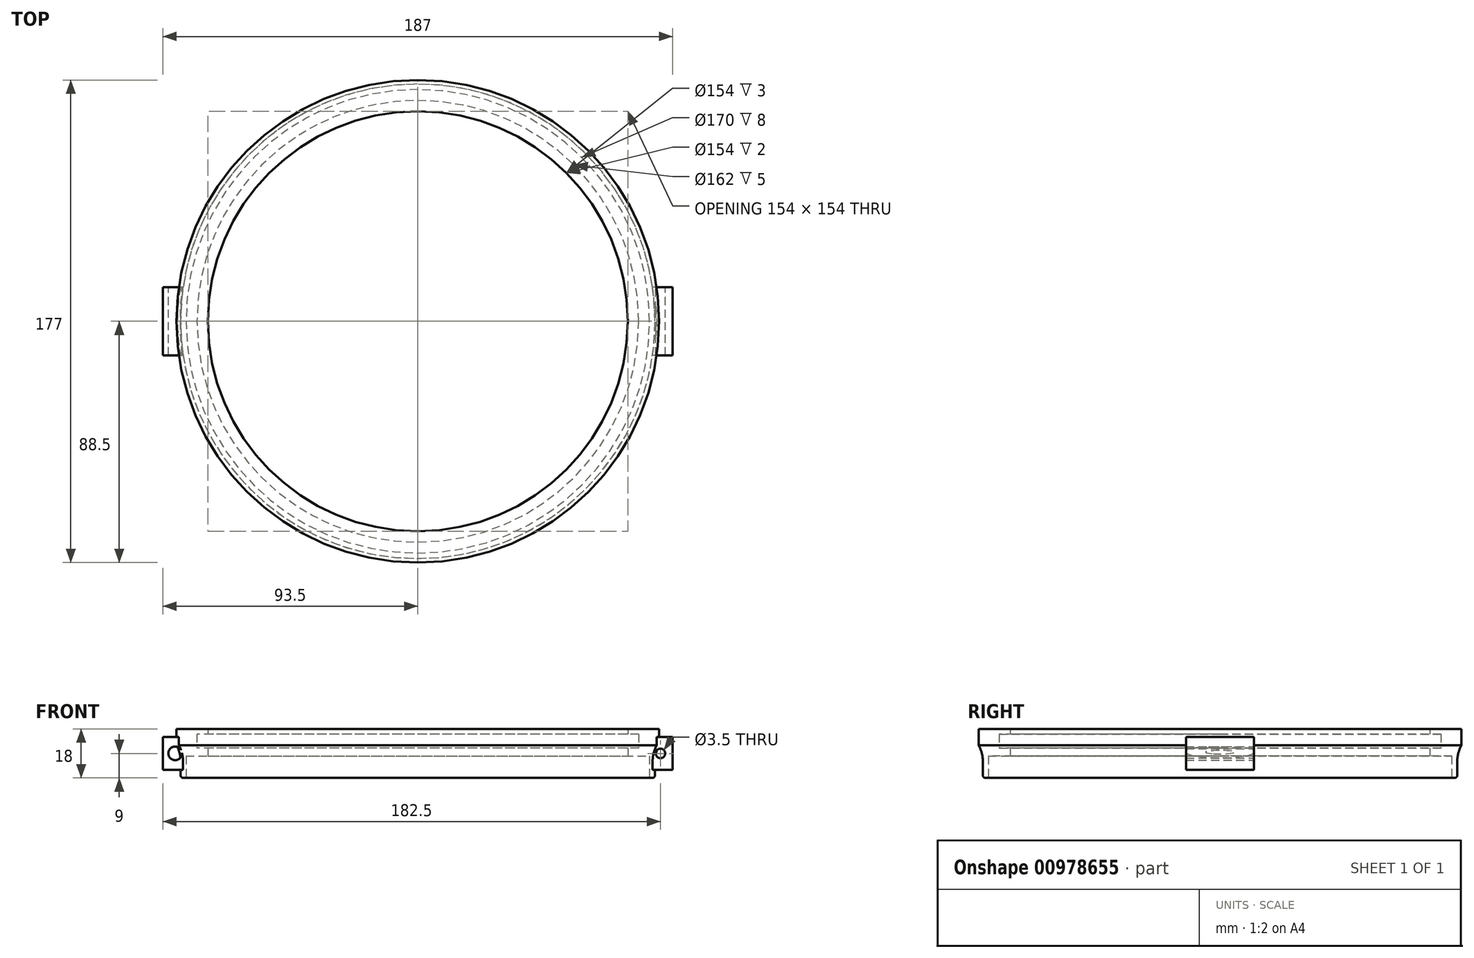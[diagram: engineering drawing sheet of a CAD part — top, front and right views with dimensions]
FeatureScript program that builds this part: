
annotation { "Feature Type Name" : "Feature", "Feature Type Description" : "" }
export const myFeature = defineFeature(function(context is Context, id is Id, definition is map)
    precondition{}
    {
        {
            var Q0;
            Q0=qCreatedBy(makeId("Front.planeOp"),FACE);
            var sketch = newSketch(context, id + "F0", { "sketchPlane" : qUnion([Q0])});
            skLineSegment(sketch, "E0", {"start": v(0, 0) * mm, "end": v(-84, 0) * mm});
            skLineSegment(sketch, "E1", {"start": v(-77, -3) * mm, "end": v(-85, -3) * mm});
            skLineSegment(sketch, "E2", {"start": v(-85, -3) * mm, "end": v(-85, -11) * mm});
            skLineSegment(sketch, "E3", {"start": v(-85, -11) * mm, "end": v(-87, -11) * mm});
            skLineSegment(sketch, "E4", {"start": v(-77, 7) * mm, "end": v(-88.5, 7) * mm});
            skLineSegment(sketch, "E5", {"start": v(-87, -11) * mm, "end": v(-87, -5) * mm});
            skLineSegment(sketch, "E6", {"start": v(-88.5, 7) * mm, "end": v(-88.5, 1) * mm});
            skArc(sketch, "E7", {"start": v(-87, -5) * mm, "mid": v(-87.38, -1.9) * mm, "end": v(-88.5, 1) * mm});
            skLineSegment(sketch, "E8", {"start": v(-77, 7) * mm, "end": v(-77, -3) * mm});
            skLineSegment(sketch, "E9", {"start": v(0, -15.27) * mm, "end": v(0, 14.73) * mm});
            skSolve(sketch);
        }
        {
            var Q0;
            Q0 = qSketchRegion(id + "F0", true);
            var Q1;
            Q1=sQuery(id+"F0.wireOp",EDGE,"E9");
            revolve(context, id + "F1", {"surfaceOperationType" : NewSurfaceOperationType.NEW, "entities" : qUnion([Q0]), "axis" : qUnion([Q1]), "revolveType" : RevolveType.FULL});
        }
        {
            var Q0;
            Q0=qCreatedBy(makeId("Top.planeOp"),FACE);
            var sketch = newSketch(context, id + "F2", { "sketchPlane" : qUnion([Q0])});
            skCircle(sketch, "E10", {"center": v(0, 0) * mm, "radius": 81 * mm});
            skSolve(sketch);
        }
        {
            var Q0;
            Q0 = qSketchRegion(id + "F2", true);
            extrude(context, id + "F3", {"entities" : qUnion([Q0]), "operationType" : NewBodyOperationType.REMOVE, "depth" : 5 * mm, "offsetDistance" : 25 * mm});
        }
        {
            var Q0;
            Q0=makeQuery(id+"F1.opRevolve","SWEPT_EDGE",EDGE,{"disambiguationData":[OSD([sQuery(id+"F0.wireOp",EDGE,"E3"),sQuery(id+"F0.wireOp",EDGE,"E5")])]});
            fillet(context, id + "F4", {"entities" : qUnion([Q0]), "radius" : 1 * mm, "tangentPropagation" : true, "allowEdgeOverflow" : false});
        }
        {
            var Q0;
            Q0=qCreatedBy(makeId("Front.planeOp"),FACE);
            var sketch = newSketch(context, id + "F5", { "sketchPlane" : qUnion([Q0])});
            skLineSegment(sketch, "E11.bottom", {"start": v(-85.5, 4) * mm, "end": v(-93.5, 4) * mm});
            skLineSegment(sketch, "E11.top", {"start": v(-85.5, -8) * mm, "end": v(-93.5, -8) * mm});
            skLineSegment(sketch, "E11.left", {"start": v(-85.5, 4) * mm, "end": v(-85.5, -8) * mm});
            skLineSegment(sketch, "E11.right", {"start": v(-93.5, 4) * mm, "end": v(-93.5, -8) * mm});
            skCircle(sketch, "E12", {"center": v(-89, -2) * mm, "radius": 2.5 * mm});
            skSolve(sketch);
        }
        {
            var Q0;
            Q0=qCreatedBy(makeId("Front.planeOp"),FACE);
            var sketch = newSketch(context, id + "F6", { "sketchPlane" : qUnion([Q0])});
            skLineSegment(sketch, "E13.bottom", {"start": v(93.5, 4) * mm, "end": v(85.5, 4) * mm});
            skLineSegment(sketch, "E13.top", {"start": v(93.5, -8) * mm, "end": v(85.5, -8) * mm});
            skLineSegment(sketch, "E13.left", {"start": v(93.5, 4) * mm, "end": v(93.5, -8) * mm});
            skLineSegment(sketch, "E13.right", {"start": v(85.5, 4) * mm, "end": v(85.5, -8) * mm});
            skCircle(sketch, "E14", {"center": v(89, -2) * mm, "radius": 1.75 * mm});
            skSolve(sketch);
        }
        {
            var Q0;
            Q0 = qSketchRegion(id + "F5", true);
            extrude(context, id + "F7", {"entities" : qUnion([Q0]), "operationType" : NewBodyOperationType.ADD, "endBound" : BoundingType.SYMMETRIC, "depth" : 25 * mm, "offsetDistance" : 25 * mm});
        }
        {
            var Q0;
            Q0 = qSketchRegion(id + "F6", true);
            extrude(context, id + "F8", {"entities" : qUnion([Q0]), "operationType" : NewBodyOperationType.ADD, "endBound" : BoundingType.SYMMETRIC, "depth" : 25 * mm, "offsetDistance" : 25 * mm});
        }
    });
